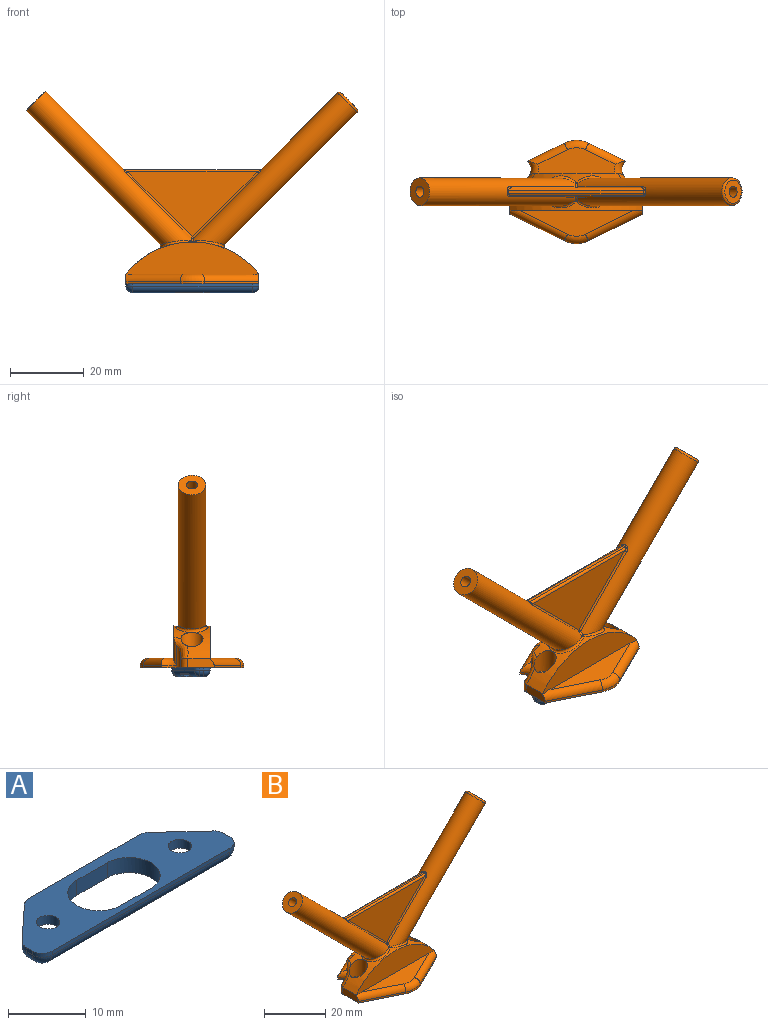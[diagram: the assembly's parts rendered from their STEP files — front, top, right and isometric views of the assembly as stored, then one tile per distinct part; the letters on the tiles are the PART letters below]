
ASSEMBLY  parts=2 mates=1
PART A: 49 faces, bbox 36.1x10.5x2.5 mm
  f0: plane 4.77x2.48mm, normal (0,0,-1), area 4.6mm2, adj f27,f28,f34,f35,f41
  f1: plane 6.96x6.81mm, normal (0,0,-1), area 24.7mm2, adj f9,f24,f25,f26,f34,f41,f46
  f2: plane 6.96x6.81mm, normal (0,0,-1), area 24.7mm2, adj f11,f18,f19,f20,f34,f45,f46
  f3: plane 4.77x2.48mm, normal (0,0,-1), area 4.6mm2, adj f17,f22,f34,f40,f45
  f4: plane 20.14x0.6mm, normal (0,1,0), area 12.1mm2, adj f16,f42,f46,f48
  f5: plane 6.13x5.69mm, normal (-0.68,0.73,0), area 5mm2, adj f16,f39,f45,f48
  f6: plane 1.12x0.6mm, normal (-1,0,0), area 0.7mm2, adj f16,f33,f39,f40
  f7: plane 32.4x0.6mm, normal (0,-1,0), area 19.4mm2, adj f16,f31,f33,f34
  f8: plane 1.12x0.6mm, normal (1,0,0), area 0.7mm2, adj f16,f31,f35,f36
  f9: cylinder r=4mm len=8mm, axis (0,0,-1), area 29.8mm2, adj f1,f10,f14,f16,f34,f46
  f10: plane 5.5x2.16mm, normal (0,1,0), area 11.9mm2, adj f9,f11,f16,f34
  f11: cylinder r=4mm len=8mm, axis (0,0,-1), area 29.8mm2, adj f2,f10,f14,f16,f34,f46
  f12: cylinder r=1.5mm len=3mm, axis (0,0,-1), area 13.2mm2, adj f16,f30
  f13: plane 6.13x5.69mm, normal (0.68,0.73,0), area 5mm2, adj f16,f36,f41,f42
  f14: plane 5.5x2.38mm, normal (0,-1,0), area 13.1mm2, adj f9,f11,f16,f46
  f15: cylinder r=1.5mm len=3mm, axis (0,0,-1), area 13.2mm2, adj f16,f23
  f16: plane 36x10.41mm, normal (0,0,1), area 216.1mm2, adj f4,f5,f6,f7,f8,f9,f10,f11
  f17: plane 3.09x1mm, normal (0.29,0.96,0), area 3.2mm2, adj f3,f18,f22,f23,f34
  f18: plane 2.37x2.2mm, normal (-0.68,0.73,0), area 3.2mm2, adj f2,f17,f19,f23,f34
  f19: plane 3.15x1mm, normal (-0.97,-0.22,0), area 3.2mm2, adj f2,f18,f20,f23
  f20: plane 3.18x1.09mm, normal (-0.29,-0.96,0), area 2.9mm2, adj f2,f19,f21,f23,f45
  f21: plane 2.37x2.2mm, normal (0.68,-0.73,0), area 1.1mm2, adj f20,f22,f23,f45
  f22: plane 3.24x1.09mm, normal (0.97,0.22,0), area 2.9mm2, adj f3,f17,f21,f23,f45
  f23: plane 6.3x6.18mm, normal (0,0,-1), area 20.1mm2, adj f15,f17,f18,f19,f20,f21,f22
  f24: plane 3.18x1.09mm, normal (0.29,-0.96,0), area 2.9mm2, adj f1,f25,f29,f30,f41
  f25: plane 3.15x1mm, normal (0.97,-0.22,0), area 3.2mm2, adj f1,f24,f26,f30
  f26: plane 2.37x2.2mm, normal (0.68,0.73,0), area 3.2mm2, adj f1,f25,f27,f30,f34
  f27: plane 3.09x1mm, normal (-0.29,0.96,0), area 3.2mm2, adj f0,f26,f28,f30,f34
  f28: plane 3.24x1.09mm, normal (-0.97,0.22,0), area 2.9mm2, adj f0,f27,f29,f30,f41
  f29: plane 2.37x2.2mm, normal (-0.68,-0.73,0), area 1.1mm2, adj f24,f28,f30,f41
  f30: plane 6.3x6.18mm, normal (0,0,-1), area 20.1mm2, adj f12,f24,f25,f26,f27,f28,f29
  f31: cylinder r=1.8mm len=1.8mm, axis (0,0,-1), area 1.7mm2, adj f7,f8,f16,f32
  f32: sphere r=1.8mm, area 5.1mm2, adj f31,f34,f35
  f33: cylinder r=1.8mm len=1.8mm, axis (0,0,1), area 1.7mm2, adj f6,f7,f16,f37
  f34: cylinder r=1.8mm len=32.4mm, axis (1,0,0), area 83.3mm2, adj f0,f1,f2,f3,f7,f9,f10,f11
  f35: cylinder r=1.8mm len=1.8mm, axis (0,1,0), area 3.2mm2, adj f0,f8,f32,f38
  f36: cylinder r=1.8mm len=1.32mm, axis (0,0,-1), area 0.9mm2, adj f8,f13,f16,f38
  f37: sphere r=1.8mm, area 5.1mm2, adj f33,f34,f40
  f38: sphere r=1.8mm, area 2.7mm2, adj f35,f36,f41
  f39: cylinder r=1.8mm len=1.32mm, axis (0,0,-1), area 0.9mm2, adj f5,f6,f16,f43
  f40: cylinder r=1.8mm len=1.8mm, axis (0,-1,0), area 3.2mm2, adj f3,f6,f37,f43
  f41: cylinder r=1.8mm len=7.35mm, axis (-0.73,0.68,0), area 17.2mm2, adj f0,f1,f13,f24,f28,f29,f38,f44
  f42: cylinder r=1.8mm len=1.22mm, axis (0,0,1), area 0.8mm2, adj f4,f13,f16,f44
  f43: sphere r=1.8mm, area 2.7mm2, adj f39,f40,f45
  f44: sphere r=1.8mm, area 2.4mm2, adj f41,f42,f46
  f45: cylinder r=1.8mm len=7.35mm, axis (-0.73,-0.68,0), area 17.2mm2, adj f2,f3,f5,f20,f21,f22,f43,f47
  f46: cylinder r=1.8mm len=20.14mm, axis (-1,0,0), area 54.7mm2, adj f1,f2,f4,f9,f11,f14,f44,f47
  f47: sphere r=1.8mm, area 2.4mm2, adj f45,f46,f48
  f48: cylinder r=1.8mm len=1.22mm, axis (0,0,-1), area 0.8mm2, adj f4,f5,f16,f47
PART B: 77 faces, bbox 90.4x29.5x53.2 mm
  f0: plane 36x28mm, normal (0,0,-1), area 593mm2, adj f6,f7,f9,f10,f11,f12,f13,f14
  f1: cylinder r=22.85mm len=36mm, axis (0,1,0), area 160.2mm2, adj f6,f8,f9,f20,f31,f33,f40,f41
  f2: cylinder r=1.5mm len=44.55mm, axis (-0.71,0,-0.71), area 556.5mm2, adj f21,f24,f25
  f3: cylinder r=1.5mm len=7.07mm, axis (-0.71,0,-0.71), area 37.3mm2, adj f24,f25,f28,f74
  f4: cylinder r=3.75mm len=44.85mm, axis (-0.71,0,-0.71), area 1180.5mm2, adj f54,f55,f57,f60,f61,f65,f67,f68
  f5: plane 20.94x7mm, normal (0,0,1), area 104mm2, adj f8,f43,f45,f47,f49,f50
  f6: plane 7.32x2.81mm, normal (1,0,0), area 17.7mm2, adj f0,f1,f12,f20,f40,f53
  f7: plane 9.98x4.91mm, normal (0.44,0.9,0), area 6.7mm2, adj f0,f13,f22,f45
  f8: plane 22.63x9.01mm, normal (0,1,0), area 176.7mm2, adj f1,f5,f42,f43,f48,f50
  f9: plane 7.32x2.81mm, normal (-1,0,0), area 17.7mm2, adj f0,f1,f10,f20,f44,f51
  f10: plane 14.69x7.23mm, normal (-0.44,-0.9,0), area 9.8mm2, adj f0,f9,f11,f51
  f11: cylinder r=7.5mm len=6.62mm, axis (0,0,-1), area 4.1mm2, adj f0,f10,f12,f52
  f12: plane 14.69x7.23mm, normal (0.44,-0.9,0), area 9.8mm2, adj f0,f6,f11,f53
  f13: cylinder r=7.5mm len=6.62mm, axis (0,0,-1), area 4.1mm2, adj f0,f7,f18,f47
  f14: plane 5.5x3mm, normal (0,1,0), area 16.5mm2, adj f0,f15,f17,f30
  f15: cylinder r=4mm len=8mm, axis (0,0,-1), area 37.7mm2, adj f0,f14,f16,f30
  f16: plane 5.5x3mm, normal (0,-1,0), area 16.5mm2, adj f0,f15,f17,f30
  f17: cylinder r=4mm len=8mm, axis (0,0,-1), area 37.7mm2, adj f0,f14,f16,f30
  f18: plane 9.98x4.91mm, normal (-0.44,0.9,0), area 6.7mm2, adj f0,f13,f23,f49
  f19: plane 31.01x7mm, normal (0,0,1), area 117.2mm2, adj f20,f51,f52,f53
  f20: plane 36.1x9.21mm, normal (0,-1,0), area 220.9mm2, adj f1,f6,f9,f19,f51,f53
  f21: plane 6.3x4.45mm, normal (0.71,0,0.71), area 24.1mm2, adj f2,f76
  f22: cylinder r=3mm len=6.04mm, axis (0,0,1), area 16.5mm2, adj f0,f7,f40,f41,f42,f43
  f23: cylinder r=3mm len=6.04mm, axis (0,0,1), area 16.5mm2, adj f0,f18,f44,f46,f48,f50
  f24: cylinder r=1.5mm len=7.07mm, axis (0.71,0,-0.71), area 37.3mm2, adj f2,f3,f29,f75
  f25: cylinder r=1.5mm len=44.55mm, axis (0.71,0,-0.71), area 557.5mm2, adj f2,f3,f27
  f26: cylinder r=3.75mm len=45.28mm, axis (0.71,0,-0.71), area 1194.6mm2, adj f27,f55,f59,f63,f66,f67,f70,f72
  f27: plane 7.5x5.3mm, normal (-0.71,0,0.71), area 37.1mm2, adj f25,f26
  f28: plane 2.81x0.44mm, normal (0.71,0,0.71), area 0.3mm2, adj f3,f30,f74
  f29: plane 2.81x0.44mm, normal (-0.71,0,0.71), area 0.3mm2, adj f24,f30,f75
  f30: plane 13.5x8mm, normal (0,0,-1), area 57.2mm2, adj f14,f15,f16,f17,f28,f29,f74,f75
  f31: cylinder r=3mm len=7.03mm, axis (0,0,-1), area 100.3mm2, adj f1,f32,f46
  f32: plane 6x6mm, normal (0,0,1), area 21.2mm2, adj f31,f36
  f33: cylinder r=3mm len=7.03mm, axis (0,0,-1), area 100.2mm2, adj f1,f34,f41
  f34: plane 6x6mm, normal (0,0,1), area 21.2mm2, adj f33,f35
  f35: cylinder r=1.5mm len=3mm, axis (0,0,1), area 23.6mm2, adj f0,f34
  f36: cylinder r=1.5mm len=3mm, axis (0,0,1), area 23.6mm2, adj f0,f32
  f37: plane 36.61x0.8mm, normal (0,0,1), area 29.3mm2, adj f61,f62,f69,f70
  f38: plane 35.02x17.51mm, normal (0,-1,0), area 306.6mm2, adj f54,f62,f63
  f39: plane 35.02x17.51mm, normal (0,1,0), area 306.6mm2, adj f68,f69,f73
  f40: cylinder r=2mm len=2.61mm, axis (0,0,1), area 8.2mm2, adj f0,f1,f6,f22,f41
  f41: bspline ~7.79x7.36mm, area 20.3mm2, adj f1,f22,f33,f40,f42
  f42: cylinder r=2mm len=7.78mm, axis (0,0,1), area 10.7mm2, adj f1,f8,f22,f41,f43
  f43: torus R=5mm, axis (0,0,1), area 10.7mm2, adj f5,f8,f22,f42,f45
  f44: cylinder r=2mm len=2.61mm, axis (0,0,1), area 8.2mm2, adj f0,f1,f9,f23,f46
  f45: cylinder r=2mm len=10.86mm, axis (0.9,-0.44,0), area 31.6mm2, adj f5,f7,f43,f47
  f46: bspline ~7.79x7.36mm, area 20.3mm2, adj f1,f23,f31,f44,f48
  f47: torus R=5.5mm, axis (0,0,1), area 19.5mm2, adj f5,f13,f45,f49
  f48: cylinder r=2mm len=7.78mm, axis (0,0,1), area 10.7mm2, adj f1,f8,f23,f46,f50
  f49: cylinder r=2mm len=10.86mm, axis (0.9,0.44,0), area 31.6mm2, adj f5,f18,f47,f50
  f50: torus R=5mm, axis (0,0,1), area 10.7mm2, adj f5,f8,f23,f48,f49
  f51: cylinder r=2mm len=15.97mm, axis (-0.9,0.44,0), area 51.1mm2, adj f9,f10,f19,f20,f52
  f52: torus R=5.5mm, axis (0,0,1), area 19.5mm2, adj f11,f19,f51,f53
  f53: cylinder r=2mm len=15.97mm, axis (-0.9,-0.44,0), area 51.1mm2, adj f6,f12,f19,f20,f52
  f54: cylinder r=0.6mm len=17.9mm, axis (-0.71,0,-0.71), area 17.7mm2, adj f4,f38,f57,f58
  f55: bspline ~1.64x1.35mm, area 0.9mm2, adj f4,f26,f56,f58
  f56: sphere r=0.6mm, area 0.3mm2, adj f55,f59,f60
  f57: bspline ~1.48x1.41mm, area 0.9mm2, adj f4,f54,f61,f62
  f58: sphere r=0.6mm, area 0.2mm2, adj f54,f55,f63
  f59: bspline ~9.58x8.7mm, area 21.6mm2, adj f1,f26,f56,f64
  f60: bspline ~9.5x8.71mm, area 21.6mm2, adj f1,f4,f56,f64
  f61: bspline ~0.8x0.45mm, area 0.4mm2, adj f4,f37,f57,f65
  f62: cylinder r=0.6mm len=36.61mm, axis (1,0,0), area 33.8mm2, adj f37,f38,f57,f66
  f63: cylinder r=0.6mm len=17.9mm, axis (0.71,0,-0.71), area 17.7mm2, adj f26,f38,f58,f66
  f64: sphere r=0.6mm, area 0.3mm2, adj f59,f60,f67
  f65: bspline ~1.64x1.55mm, area 0.9mm2, adj f4,f61,f68,f69
  f66: bspline ~1.64x1.55mm, area 0.9mm2, adj f26,f62,f63,f70
  f67: bspline ~1.64x1.35mm, area 0.9mm2, adj f4,f26,f64,f71
  f68: cylinder r=0.6mm len=17.9mm, axis (-0.71,0,-0.71), area 17.7mm2, adj f4,f39,f65,f71
  f69: cylinder r=0.6mm len=36.61mm, axis (-1,0,0), area 33.8mm2, adj f37,f39,f65,f72
  f70: bspline ~0.8x0.45mm, area 0.4mm2, adj f26,f37,f66,f72
  f71: sphere r=0.6mm, area 0.2mm2, adj f67,f68,f73
  f72: bspline ~1.48x1.41mm, area 0.9mm2, adj f26,f69,f70,f73
  f73: cylinder r=0.6mm len=17.9mm, axis (0.71,0,-0.71), area 17.7mm2, adj f26,f39,f71,f72
  f74: bspline ~5.94x4.2mm, area 12.1mm2, adj f3,f28,f30
  f75: bspline ~5.94x4.2mm, area 12.1mm2, adj f24,f29,f30
  f76: torus R=3.15mm, axis (-0.71,0,-0.71), area 20.9mm2, adj f4,f21
PLACE A t=(49.21,27.8,-24.36)mm
PLACE B t=(49.21,27.8,-21.96)mm
MATE fastened B.f35 <-> A.f12  axis (0,0,1) through (61.21,27.8,-21.96)mm
